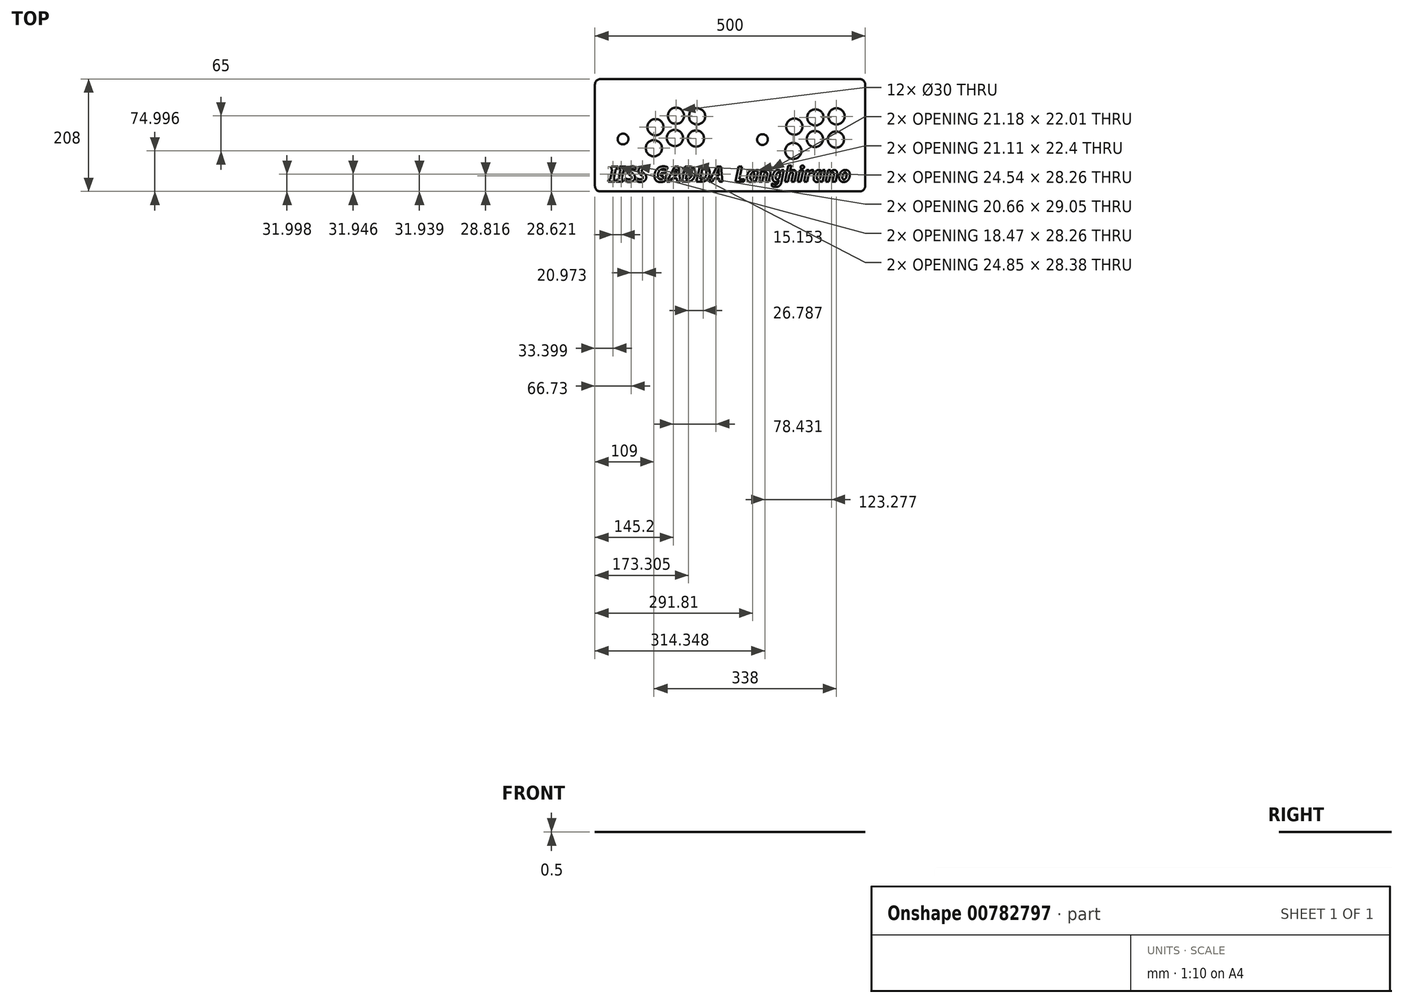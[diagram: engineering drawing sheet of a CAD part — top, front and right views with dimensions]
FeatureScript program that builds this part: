
annotation { "Feature Type Name" : "Feature", "Feature Type Description" : "" }
export const myFeature = defineFeature(function(context is Context, id is Id, definition is map)
    precondition{}
    {
        {
            assignVariable(context, id + "F0", {"name" : "SPESS_PANNELLO", "anyValue" : .5});
        }
        {
            var Q0;
            Q0=qCreatedBy(makeId("Top.planeOp"),FACE);
            var sketch = newSketch(context, id + "F1", { "sketchPlane" : qUnion([Q0])});
            skLineSegment(sketch, "E0.bottom", {"start": v(-437, 169.47) * mm, "end": v(43, 169.47) * mm});
            skLineSegment(sketch, "E0.left", {"start": v(-447, 159.47) * mm, "end": v(-447, -21.88) * mm});
            skLineSegment(sketch, "E0.right", {"start": v(53, 159.47) * mm, "end": v(53, -21.88) * mm});
            skCircle(sketch, "E1", {"center": v(-395, 58.47) * mm, "radius": 10 * mm});
            skPoint(sketch, "E2.visualSharp", {"position": v(53, -21.88) * mm});
            skPoint(sketch, "E3.visualSharp", {"position": v(-447, -21.88) * mm});
            skCircle(sketch, "E4", {"center": v(-335, 80.47) * mm, "radius": 15 * mm});
            skCircle(sketch, "E5", {"center": v(-338, 41.47) * mm, "radius": 15 * mm});
            skCircle(sketch, "E6", {"center": v(-299, 60.47) * mm, "radius": 15 * mm});
            skCircle(sketch, "E7", {"center": v(-260, 59.47) * mm, "radius": 15 * mm});
            skCircle(sketch, "E8", {"center": v(-258, 100.47) * mm, "radius": 15 * mm});
            skCircle(sketch, "E9", {"center": v(-297, 101.47) * mm, "radius": 15 * mm});
            skCircle(sketch, "E10", {"center": v(-137, 57.47) * mm, "radius": 10 * mm});
            skCircle(sketch, "E11", {"center": v(-78, 81.47) * mm, "radius": 15 * mm});
            skCircle(sketch, "E12", {"center": v(-80, 36.47) * mm, "radius": 15 * mm});
            skCircle(sketch, "E13", {"center": v(-39, 98.47) * mm, "radius": 15 * mm});
            skCircle(sketch, "E14", {"center": v(-40, 58.47) * mm, "radius": 15 * mm});
            skCircle(sketch, "E15", {"center": v(0, 100.47) * mm, "radius": 15 * mm});
            skCircle(sketch, "E16", {"center": v(-1, 57.47) * mm, "radius": 15 * mm});
            skLineSegment(sketch, "E17.0", {"start": v(-437, -38.53) * mm, "end": v(43, -38.53) * mm});
            skLineSegment(sketch, "E18", {"start": v(-447, -21.88) * mm, "end": v(-447, -28.53) * mm});
            skLineSegment(sketch, "E19", {"start": v(53, -21.88) * mm, "end": v(53, -28.53) * mm});
            skArc(sketch, "E20.filletArc", {"start": v(-447, -28.53) * mm, "mid": v(-444.07, -35.6) * mm, "end": v(-437, -38.53) * mm});
            skArc(sketch, "E21.filletArc", {"start": v(43, -38.53) * mm, "mid": v(50.07, -35.6) * mm, "end": v(53, -28.53) * mm});
            skArc(sketch, "E22.filletArc", {"start": v(53, 159.47) * mm, "mid": v(50.07, 166.54) * mm, "end": v(43, 169.47) * mm});
            skArc(sketch, "E23.filletArc", {"start": v(-437, 169.47) * mm, "mid": v(-444.07, 166.54) * mm, "end": v(-447, 159.47) * mm});
            skSolve(sketch);
        }
        {
            var Q0;
            Q0=makeQuery(id+"F1.imprint","IMPRINT",FACE,{"disambiguationData":[TD([[makeQuery(id+"F1.imprint","IMPRINT",EDGE,{"derivedFrom":sQuery(id+"F1.wireOp",EDGE,"E0.bottom")}),-1.0]])]});
            var Q1;
            Q1=makeQuery(id+"F1.imprint","IMPRINT",FACE,{"disambiguationData":[TD([[makeQuery(id+"F1.imprint","IMPRINT",EDGE,{"derivedFrom":sQuery(id+"F1.wireOp",EDGE,"E0.top")}),-1.0]])]});
            var Q2;
            {var subQ0=sQuery(id+"F1.wireOp",EDGE,"E18");Q2=makeQuery(id+"F1.imprint","IMPRINT",FACE,{"disambiguationData":[TD([[makeQuery(id+"F1.imprint","IMPRINT",EDGE,{"derivedFrom":subQ0}),1.0]])]});}
            var Q3;
            {var subQ1=sQuery(id+"F1.wireOp",EDGE,"E19");Q3=makeQuery(id+"F1.imprint","IMPRINT",FACE,{"disambiguationData":[TD([[makeQuery(id+"F1.imprint","IMPRINT",EDGE,{"derivedFrom":subQ1}),-1.0]])]});}
            extrude(context, id + "F2", {"entities" : qUnion([Q0, Q1, Q2, Q3]), "depth" : (getVariable(context, 'SPESS_PANNELLO')) * mm, "offsetDistance" : 25 * mm});
        }
        {
            var Q0;
            Q0=makeQuery(id+"F2.opExtrude","CAP_FACE",FACE,{"disambiguationData":[OSD([sQuery(id+"F1.wireOp",EDGE,"E0.bottom"),sQuery(id+"F1.wireOp",EDGE,"E0.left"),sQuery(id+"F1.wireOp",EDGE,"E0.right"),sQuery(id+"F1.wireOp",EDGE,"E1"),sQuery(id+"F1.wireOp",EDGE,"E4"),sQuery(id+"F1.wireOp",EDGE,"E5"),sQuery(id+"F1.wireOp",EDGE,"E6"),sQuery(id+"F1.wireOp",EDGE,"E7"),sQuery(id+"F1.wireOp",EDGE,"E8"),sQuery(id+"F1.wireOp",EDGE,"E9"),sQuery(id+"F1.wireOp",EDGE,"E10"),sQuery(id+"F1.wireOp",EDGE,"E11"),sQuery(id+"F1.wireOp",EDGE,"E12"),sQuery(id+"F1.wireOp",EDGE,"E13"),sQuery(id+"F1.wireOp",EDGE,"E14"),sQuery(id+"F1.wireOp",EDGE,"E15"),sQuery(id+"F1.wireOp",EDGE,"E16"),sQuery(id+"F1.wireOp",EDGE,"E17.0"),sQuery(id+"F1.wireOp",EDGE,"E18"),sQuery(id+"F1.wireOp",EDGE,"E19"),sQuery(id+"F1.wireOp",EDGE,"E20.filletArc"),sQuery(id+"F1.wireOp",EDGE,"E21.filletArc"),sQuery(id+"F1.wireOp",EDGE,"E22.filletArc"),sQuery(id+"F1.wireOp",EDGE,"E23.filletArc")])],"isStart":false});
            var sketch = newSketch(context, id + "F3", { "sketchPlane" : qUnion([Q0])});
            skText(sketch, "E24", { "text": "IISS GADDA  Langhirano", "fontName": "NotoSans-BoldItalic.ttf"});
            const initialGuessF3  = {"E24": [-0.4217, -0.02072, 1, 0, 0.0285]};
            skSetInitialGuess(sketch, initialGuessF3);
            skSolve(sketch);
        }
        {
            var Q0;
            Q0 = qSketchRegion(id + "F3", true);
            extrude(context, id + "F4", {"entities" : qUnion([Q0]), "operationType" : NewBodyOperationType.REMOVE, "oppositeDirection" : true, "depth" : 1 * mm, "offsetDistance" : 25 * mm});
        }
    });
